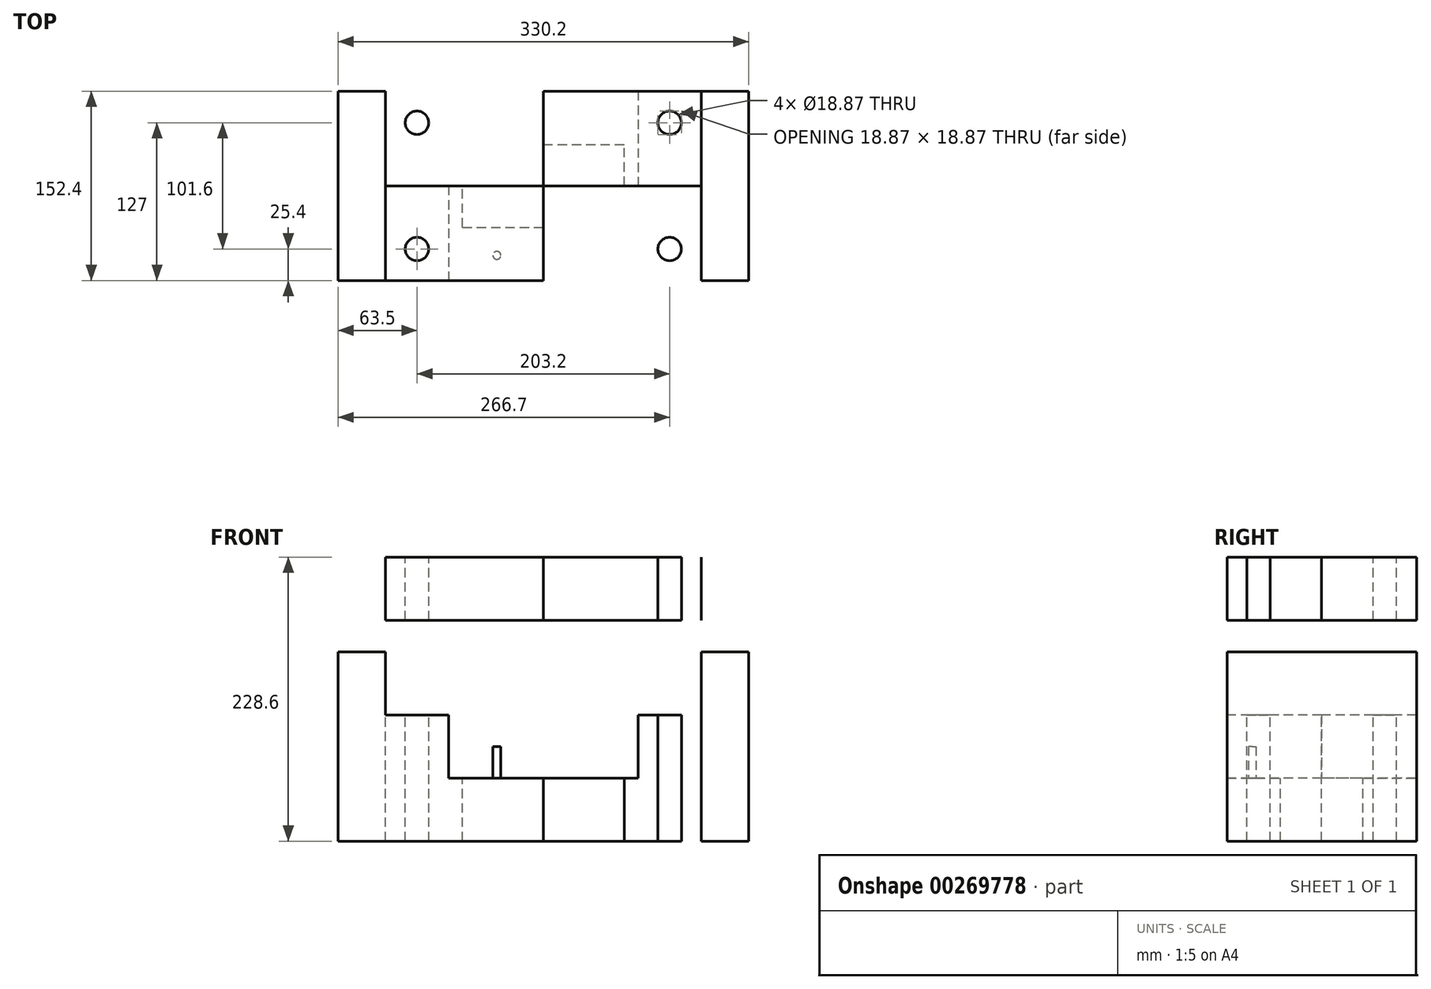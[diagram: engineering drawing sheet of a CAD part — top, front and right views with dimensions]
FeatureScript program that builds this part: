
annotation { "Feature Type Name" : "Feature", "Feature Type Description" : "" }
export const myFeature = defineFeature(function(context is Context, id is Id, definition is map)
    precondition{}
    {
        {
            var Q0;
            Q0=qCreatedBy(makeId("Front.planeOp"),FACE);
            var sketch = newSketch(context, id + "F6", { "sketchPlane" : qUnion([Q0])});
            skLineSegment(sketch, "E0.bottom", {"start": v(0, 0) * mm, "end": v(38.1, 0) * mm});
            skLineSegment(sketch, "E0.top", {"start": v(0, 152.4) * mm, "end": v(38.1, 152.4) * mm});
            skLineSegment(sketch, "E0.left", {"start": v(0, 0) * mm, "end": v(0, 152.4) * mm});
            skLineSegment(sketch, "E0.right", {"start": v(38.1, 0) * mm, "end": v(38.1, 152.4) * mm});
            skLineSegment(sketch, "E1.bottom", {"start": v(38.1, 0) * mm, "end": v(88.9, 0) * mm});
            skLineSegment(sketch, "E1.top", {"start": v(38.1, 101.6) * mm, "end": v(88.9, 101.6) * mm});
            skLineSegment(sketch, "E1.left", {"start": v(38.1, 0) * mm, "end": v(38.1, 101.6) * mm});
            skLineSegment(sketch, "E1.right", {"start": v(88.9, 0) * mm, "end": v(88.9, 101.6) * mm});
            skLineSegment(sketch, "E2.bottom", {"start": v(88.9, 0) * mm, "end": v(165.1, 0) * mm});
            skLineSegment(sketch, "E2.top", {"start": v(88.9, 50.8) * mm, "end": v(165.1, 50.8) * mm});
            skLineSegment(sketch, "E2.left", {"start": v(88.9, 0) * mm, "end": v(88.9, 50.8) * mm});
            skLineSegment(sketch, "E2.right", {"start": v(165.1, 0) * mm, "end": v(165.1, 50.8) * mm});
            skLineSegment(sketch, "E3.MirrorCS", {"start": v(330.2, 0) * mm, "end": v(330.2, 152.4) * mm});
            skLineSegment(sketch, "E4.MirrorCS", {"start": v(292.1, 0) * mm, "end": v(292.1, 152.4) * mm});
            skLineSegment(sketch, "E5.MirrorCS", {"start": v(292.1, 0) * mm, "end": v(241.3, 0) * mm});
            skLineSegment(sketch, "E6.MirrorCS", {"start": v(330.2, 0) * mm, "end": v(292.1, 0) * mm});
            skLineSegment(sketch, "E7.MirrorCS", {"start": v(292.1, 101.6) * mm, "end": v(241.3, 101.6) * mm});
            skLineSegment(sketch, "E8.MirrorCS", {"start": v(330.2, 152.4) * mm, "end": v(292.1, 152.4) * mm});
            skLineSegment(sketch, "E9.MirrorCS", {"start": v(241.3, 50.8) * mm, "end": v(165.1, 50.8) * mm});
            skLineSegment(sketch, "E10.MirrorCS", {"start": v(241.3, 0) * mm, "end": v(165.1, 0) * mm});
            skLineSegment(sketch, "E11.MirrorCS", {"start": v(241.3, 0) * mm, "end": v(241.3, 101.6) * mm});
            skSolve(sketch);
        }
        {
            var Q0;
            Q0=makeQuery(id+"F6.imprint","IMPRINT",FACE,{"disambiguationData":[TD([[makeQuery(id+"F6.imprint","IMPRINT",EDGE,{"derivedFrom":sQuery(id+"F6.wireOp",EDGE,"E0.bottom")}),1.0]])]});
            var Q1;
            Q1=makeQuery(id+"F6.imprint","IMPRINT",FACE,{"disambiguationData":[TD([[makeQuery(id+"F6.imprint","IMPRINT",EDGE,{"derivedFrom":sQuery(id+"F6.wireOp",EDGE,"E2.bottom")}),1.0]])]});
            var Q2;
            Q2=makeQuery(id+"F6.imprint","IMPRINT",FACE,{"disambiguationData":[TD([[makeQuery(id+"F6.imprint","IMPRINT",EDGE,{"derivedFrom":sQuery(id+"F6.wireOp",EDGE,"E1.bottom")}),1.0]])]});
            var Q3;
            Q3=makeQuery(id+"F6.imprint","IMPRINT",FACE,{"disambiguationData":[TD([[makeQuery(id+"F6.imprint","IMPRINT",EDGE,{"derivedFrom":sQuery(id+"F6.wireOp",EDGE,"E2.right")}),-1.0]])]});
            var Q4;
            {var subQ1=sQuery(id+"F6.wireOp",EDGE,"E5.MirrorCS");Q4=makeQuery(id+"F6.imprint","IMPRINT",FACE,{"disambiguationData":[TD([[makeQuery(id+"F6.imprint","IMPRINT",EDGE,{"derivedFrom":subQ1}),-1.0]])]});}
            var Q5;
            Q5=makeQuery(id+"F6.imprint","IMPRINT",FACE,{"disambiguationData":[TD([[makeQuery(id+"F6.imprint","IMPRINT",EDGE,{"derivedFrom":sQuery(id+"F6.wireOp",EDGE,"E3.MirrorCS")}),1.0]])]});
            extrude(context, id + "F7", {"entities" : qUnion([Q0, Q1, Q2, Q3, Q4, Q5]), "oppositeDirection" : true, "depth" : 152.4 * mm});
        }
        {
            var Q0;
            Q0=makeQuery(id+"F7.opExtrude","SWEPT_FACE",FACE,{"disambiguationData":[OSD([sQuery(id+"F6.wireOp",EDGE,"E2.top"),sQuery(id+"F6.wireOp",EDGE,"E9.MirrorCS")])]});
            var sketch = newSketch(context, id + "F0", { "sketchPlane" : qUnion([Q0])});
            skLineSegment(sketch, "E12.bottom", {"start": v(230.08, 109.44) * mm, "end": v(100.12, 109.44) * mm});
            skLineSegment(sketch, "E12.top", {"start": v(230.08, 42.96) * mm, "end": v(100.12, 42.96) * mm});
            skLineSegment(sketch, "E12.left", {"start": v(230.08, 109.44) * mm, "end": v(230.08, 42.96) * mm});
            skLineSegment(sketch, "E12.right", {"start": v(100.12, 109.44) * mm, "end": v(100.12, 42.96) * mm});
            skPoint(sketch, "E12.middle", {"position": v(165.1, 76.2) * mm});
            skPoint(sketch, "E12.middle.positionSnap0", {"position": v(88.9, 76.2) * mm});
            skPoint(sketch, "E12.middle.positionSnap1", {"position": v(165.1, 0) * mm});
            skPoint(sketch, "E12.centerSnap0", {"position": v(88.9, 76.2) * mm});
            skPoint(sketch, "E12.centerSnap1", {"position": v(165.1, 0) * mm});
            skSolve(sketch);
        }
        {
            var Q0;
            Q0=makeQuery(id+"F0.imprint","IMPRINT",FACE,{"disambiguationData":[TD([[makeQuery(id+"F0.imprint","IMPRINT",EDGE,{"derivedFrom":sQuery(id+"F0.wireOp",EDGE,"E12.bottom")}),1.0]])]});
            extrude(context, id + "F1", {"entities" : qUnion([Q0]), "operationType" : NewBodyOperationType.REMOVE, "endBound" : BoundingType.THROUGH_ALL, "oppositeDirection" : true, "depth" : 25.4 * mm});
        }
        {
            var Q0;
            Q0=qCreatedBy(makeId("Front.planeOp"),FACE);
            var sketch = newSketch(context, id + "F8", { "sketchPlane" : qUnion([Q0])});
            skLineSegment(sketch, "E13.bottom", {"start": v(38.1, 177.8) * mm, "end": v(292.1, 177.8) * mm});
            skLineSegment(sketch, "E13.top", {"start": v(38.1, 228.6) * mm, "end": v(292.1, 228.6) * mm});
            skLineSegment(sketch, "E13.left", {"start": v(38.1, 177.8) * mm, "end": v(38.1, 228.6) * mm});
            skLineSegment(sketch, "E13.right", {"start": v(292.1, 177.8) * mm, "end": v(292.1, 228.6) * mm});
            skLineSegment(sketch, "E14.bottom", {"start": v(165.1, 177.8) * mm, "end": v(165.1, 177.8) * mm});
            skLineSegment(sketch, "E14.top", {"start": v(165.1, 177.8) * mm, "end": v(165.1, 177.8) * mm});
            skLineSegment(sketch, "E14.left", {"start": v(165.1, 177.8) * mm, "end": v(165.1, 177.8) * mm});
            skLineSegment(sketch, "E14.right", {"start": v(165.1, 177.8) * mm, "end": v(165.1, 177.8) * mm});
            skPoint(sketch, "E14.middle", {"position": v(165.1, 177.8) * mm});
            skLineSegment(sketch, "E15.bottom", {"start": v(139.7, 177.8) * mm, "end": v(190.5, 177.8) * mm});
            skLineSegment(sketch, "E15.top", {"start": v(139.7, 152.4) * mm, "end": v(190.5, 152.4) * mm});
            skLineSegment(sketch, "E15.left", {"start": v(139.7, 177.8) * mm, "end": v(139.7, 152.4) * mm});
            skLineSegment(sketch, "E15.right", {"start": v(190.5, 177.8) * mm, "end": v(190.5, 152.4) * mm});
            skSolve(sketch);
        }
        {
            var Q0;
            Q0=makeQuery(id+"F8.imprint","IMPRINT",FACE,{"disambiguationData":[TD([[makeQuery(id+"F8.imprint","IMPRINT",EDGE,{"derivedFrom":sQuery(id+"F8.wireOp",EDGE,"E13.bottom")}),1.0]])]});
            extrude(context, id + "F9", {"entities" : qUnion([Q0]), "oppositeDirection" : true, "depth" : 152.4 * mm});
        }
        {
            var Q0;
            Q0=makeQuery(id+"F7.opExtrude","SWEPT_FACE",FACE,{"disambiguationData":[OSD([sQuery(id+"F6.wireOp",EDGE,"E2.top"),sQuery(id+"F6.wireOp",EDGE,"E9.MirrorCS")])]});
            var sketch = newSketch(context, id + "F2", { "sketchPlane" : qUnion([Q0])});
            skCircle(sketch, "E16", {"center": v(127.75, 20.32) * mm, "radius": 3.18 * mm});
            skCircle(sketch, "E17", {"center": v(200.19, 20.32) * mm, "radius": 3.18 * mm});
            skSolve(sketch);
        }
        {
            var Q0;
            Q0 = qSketchRegion(id + "F2", true);
            extrude(context, id + "F3", {"entities" : qUnion([Q0]), "operationType" : NewBodyOperationType.ADD, "depth" : 25.4 * mm});
        }
        {
            var Q0;
            Q0=makeQuery(id+"F9.opExtrude","SWEPT_FACE",FACE,{"disambiguationData":[OSD([sQuery(id+"F8.wireOp",EDGE,"E13.top")])]});
            var sketch = newSketch(context, id + "F4", { "sketchPlane" : qUnion([Q0])});
            skCircle(sketch, "E18", {"center": v(63.5, 25.4) * mm, "radius": 9.44 * mm});
            skLineSegment(sketch, "E19", {"start": v(38.1, 76.2) * mm, "end": v(38.1, 76.2) * mm});
            skLineSegment(sketch, "E20", {"start": v(38.1, 76.2) * mm, "end": v(292.1, 76.2) * mm});
            skLineSegment(sketch, "E21", {"start": v(165.1, 152.4) * mm, "end": v(165.1, 0) * mm});
            skCircle(sketch, "E22.MirrorC", {"center": v(63.5, 127) * mm, "radius": 9.44 * mm});
            skLineSegment(sketch, "E23.MirrorCS", {"start": v(165.1, 0) * mm, "end": v(165.1, 152.4) * mm});
            skCircle(sketch, "E24.MirrorC", {"center": v(266.7, 127) * mm, "radius": 9.44 * mm});
            skCircle(sketch, "E25.MirrorC", {"center": v(266.7, 25.4) * mm, "radius": 9.44 * mm});
            skSolve(sketch);
        }
        {
            var Q0;
            Q0=makeQuery(id+"F4.imprint","IMPRINT",FACE,{"disambiguationData":[TD([[makeQuery(id+"F4.imprint","IMPRINT",EDGE,{"derivedFrom":sQuery(id+"F4.wireOp",EDGE,"E18")}),1.0]])]});
            var Q1;
            Q1=makeQuery(id+"F4.imprint","IMPRINT",FACE,{"disambiguationData":[TD([[makeQuery(id+"F4.imprint","IMPRINT",EDGE,{"derivedFrom":sQuery(id+"F4.wireOp",EDGE,"E22.MirrorC")}),-1.0]])]});
            var Q2;
            Q2=makeQuery(id+"F4.imprint","IMPRINT",FACE,{"disambiguationData":[TD([[makeQuery(id+"F4.imprint","IMPRINT",EDGE,{"derivedFrom":sQuery(id+"F4.wireOp",EDGE,"E25.MirrorC")}),-1.0]])]});
            var Q3;
            Q3=makeQuery(id+"F4.imprint","IMPRINT",FACE,{"disambiguationData":[TD([[makeQuery(id+"F4.imprint","IMPRINT",EDGE,{"derivedFrom":sQuery(id+"F4.wireOp",EDGE,"E24.MirrorC")}),1.0]])]});
            extrude(context, id + "F10", {"entities" : qUnion([Q0, Q1, Q2, Q3]), "operationType" : NewBodyOperationType.REMOVE, "endBound" : BoundingType.THROUGH_ALL, "oppositeDirection" : true, "depth" : 267.53 * mm});
        }
    });
